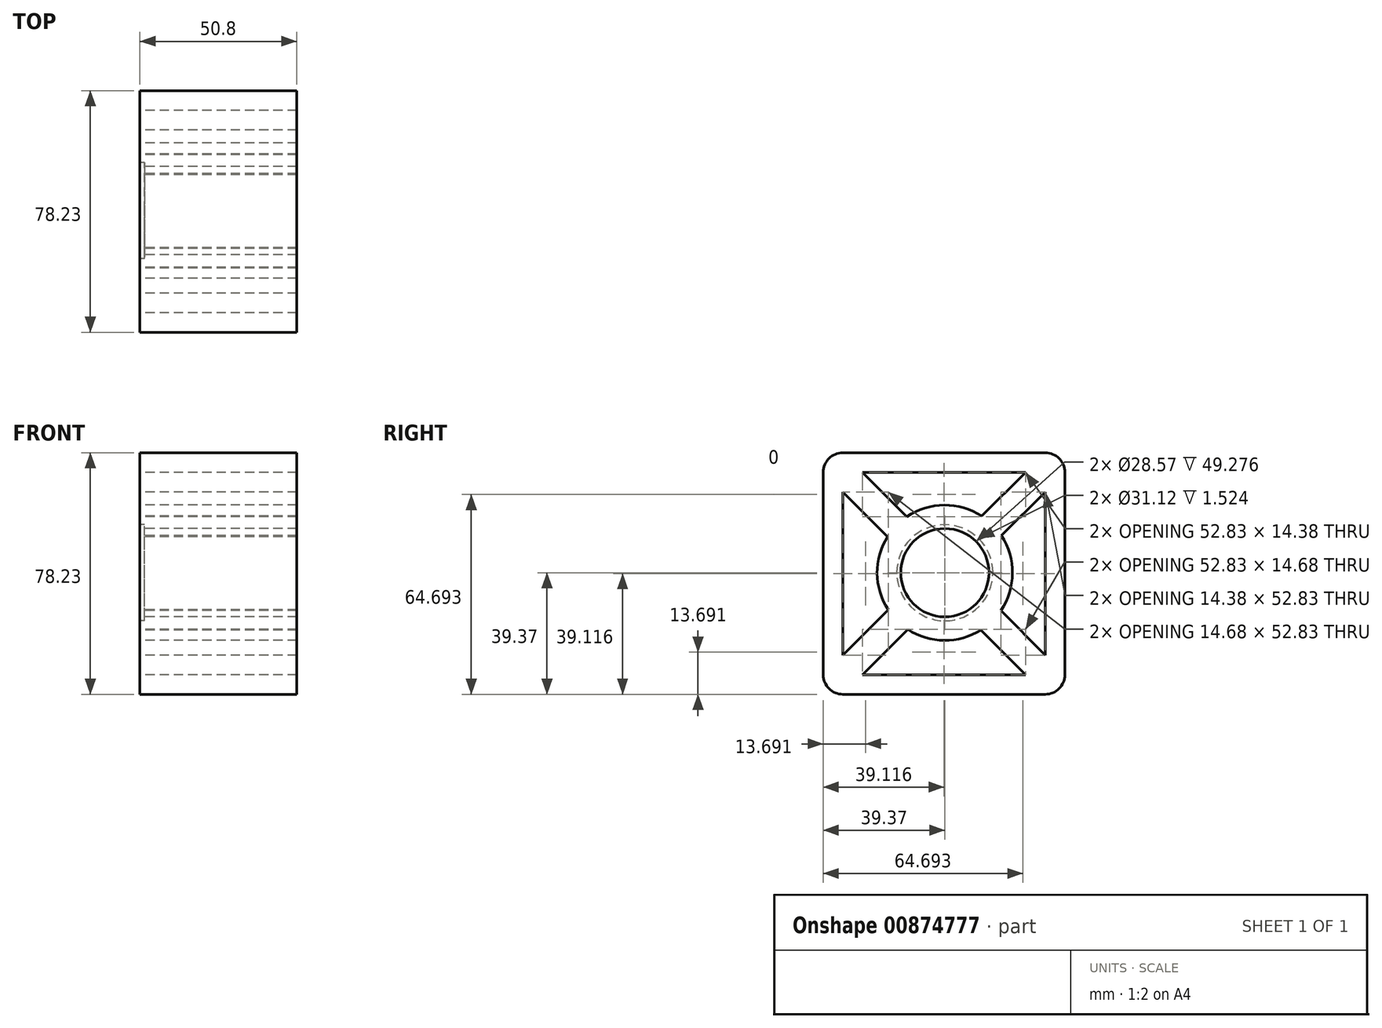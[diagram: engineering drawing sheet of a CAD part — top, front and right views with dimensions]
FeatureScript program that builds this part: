
annotation { "Feature Type Name" : "Feature", "Feature Type Description" : "" }
export const myFeature = defineFeature(function(context is Context, id is Id, definition is map)
    precondition{}
    {
        {
            var Q0;
            Q0=qCreatedBy(makeId("Right.planeOp"),FACE);
            var sketch = newSketch(context, id + "F0", { "sketchPlane" : qUnion([Q0])});
            skLineSegment(sketch, "E0.bottom", {"start": v(-33.02, 38.86) * mm, "end": v(32.51, 38.86) * mm});
            skLineSegment(sketch, "E0.top", {"start": v(-33.02, -39.37) * mm, "end": v(32.51, -39.37) * mm});
            skLineSegment(sketch, "E0.left", {"start": v(-39.37, 32.51) * mm, "end": v(-39.37, -33.02) * mm});
            skLineSegment(sketch, "E0.right", {"start": v(38.86, 32.51) * mm, "end": v(38.86, -33.02) * mm});
            skPoint(sketch, "E1.visualSharp", {"position": v(-39.37, 38.86) * mm});
            skArc(sketch, "E1.filletArc", {"start": v(-33.02, 38.86) * mm, "mid": v(-37.51, 37) * mm, "end": v(-39.37, 32.51) * mm});
            skPoint(sketch, "E2.visualSharp", {"position": v(38.86, 38.86) * mm});
            skArc(sketch, "E2.filletArc", {"start": v(38.86, 32.51) * mm, "mid": v(37, 37) * mm, "end": v(32.51, 38.86) * mm});
            skPoint(sketch, "E3.visualSharp", {"position": v(38.86, -39.37) * mm});
            skArc(sketch, "E3.filletArc", {"start": v(32.51, -39.37) * mm, "mid": v(37, -37.51) * mm, "end": v(38.86, -33.02) * mm});
            skPoint(sketch, "E4.visualSharp", {"position": v(-39.37, -39.37) * mm});
            skArc(sketch, "E4.filletArc", {"start": v(-39.37, -33.02) * mm, "mid": v(-37.51, -37.51) * mm, "end": v(-33.02, -39.37) * mm});
            skLineSegment(sketch, "E5.bottom", {"start": v(26.16, 32.51) * mm, "end": v(-26.67, 32.51) * mm});
            skLineSegment(sketch, "E5.top", {"start": v(26.16, -33.02) * mm, "end": v(-26.67, -33.02) * mm});
            skLineSegment(sketch, "E5.left", {"start": v(32.51, 26.16) * mm, "end": v(32.51, -26.67) * mm});
            skLineSegment(sketch, "E5.right", {"start": v(-33.02, 26.16) * mm, "end": v(-33.02, -26.67) * mm});
            skArc(sketch, "E6", {"start": v(11.99, 18.34) * mm, "mid": v(-0.18, 21.9) * mm, "end": v(-12.3, 18.13) * mm});
            skLineSegment(sketch, "E7", {"start": v(32.51, 26.16) * mm, "end": v(18.34, 11.99) * mm});
            skLineSegment(sketch, "E8", {"start": v(26.16, 32.51) * mm, "end": v(11.99, 18.34) * mm});
            skLineSegment(sketch, "E9", {"start": v(32.51, -26.67) * mm, "end": v(18.13, -12.3) * mm});
            skLineSegment(sketch, "E10", {"start": v(26.16, -33.02) * mm, "end": v(11.68, -18.54) * mm});
            skLineSegment(sketch, "E11.trimOffspring", {"start": v(-12.3, 18.13) * mm, "end": v(-26.67, 32.51) * mm});
            skLineSegment(sketch, "E12.trimOffspring", {"start": v(-11.99, -18.34) * mm, "end": v(-26.67, -33.02) * mm});
            skLineSegment(sketch, "E13.trimOffspring", {"start": v(-18.34, -11.99) * mm, "end": v(-33.02, -26.67) * mm});
            skLineSegment(sketch, "E14.trimOffspring", {"start": v(-18.54, 11.68) * mm, "end": v(-33.02, 26.16) * mm});
            skArc(sketch, "E15.trimOffspring", {"start": v(-18.54, 11.68) * mm, "mid": v(-21.9, -0.18) * mm, "end": v(-18.34, -11.99) * mm});
            skArc(sketch, "E16.trimOffspring", {"start": v(-11.99, -18.34) * mm, "mid": v(-0.18, -21.9) * mm, "end": v(11.68, -18.54) * mm});
            skArc(sketch, "E17.trimOffspring", {"start": v(18.13, -12.3) * mm, "mid": v(21.9, -0.18) * mm, "end": v(18.34, 11.99) * mm});
            skCircle(sketch, "E18", {"center": v(0, 0) * mm, "radius": 14.29 * mm});
            skSolve(sketch);
        }
        {
            var Q0;
            Q0=makeQuery(id+"F0.imprint","IMPRINT",FACE,{"disambiguationData":[TD([[makeQuery(id+"F0.imprint","IMPRINT",EDGE,{"derivedFrom":sQuery(id+"F0.wireOp",EDGE,"E0.bottom")}),-1.0]])]});
            extrude(context, id + "F1", {"entities" : qUnion([Q0]), "depth" : 50.8 * mm, "offsetDistance" : 25.4 * mm});
        }
        {
            var Q0;
            Q0=qCreatedBy(makeId("Right.planeOp"),FACE);
            var sketch = newSketch(context, id + "F2", { "sketchPlane" : qUnion([Q0])});
            skCircle(sketch, "E19", {"center": v(0, 0) * mm, "radius": 15.56 * mm});
            skCircle(sketch, "E20", {"center": v(0, 0) * mm, "radius": 14.29 * mm});
            skSolve(sketch);
        }
        {
            var Q0;
            {var subQ0=sQuery(id+"F0.wireOp",EDGE,"E0.right");Q0=makeQuery(id+"F0.imprint","IMPRINT",FACE,{"disambiguationData":[TD([[makeQuery(id+"F0.imprint","IMPRINT",EDGE,{"derivedFrom":subQ0}),-1.0]])]});}
            extrude(context, id + "F3", {"entities" : qUnion([Q0]), "depth" : 50.8 * mm, "offsetDistance" : 25.4 * mm});
        }
        {
            var Q0;
            Q0=makeQuery(id+"F2.imprint","IMPRINT",FACE,{"disambiguationData":[TD([[makeQuery(id+"F2.imprint","IMPRINT",EDGE,{"derivedFrom":sQuery(id+"F2.wireOp",EDGE,"E19")}),1.0]])]});
            extrude(context, id + "F4", {"entities" : qUnion([Q0]), "operationType" : NewBodyOperationType.REMOVE, "depth" : 1.52 * mm, "offsetDistance" : 25.4 * mm});
        }
    });
